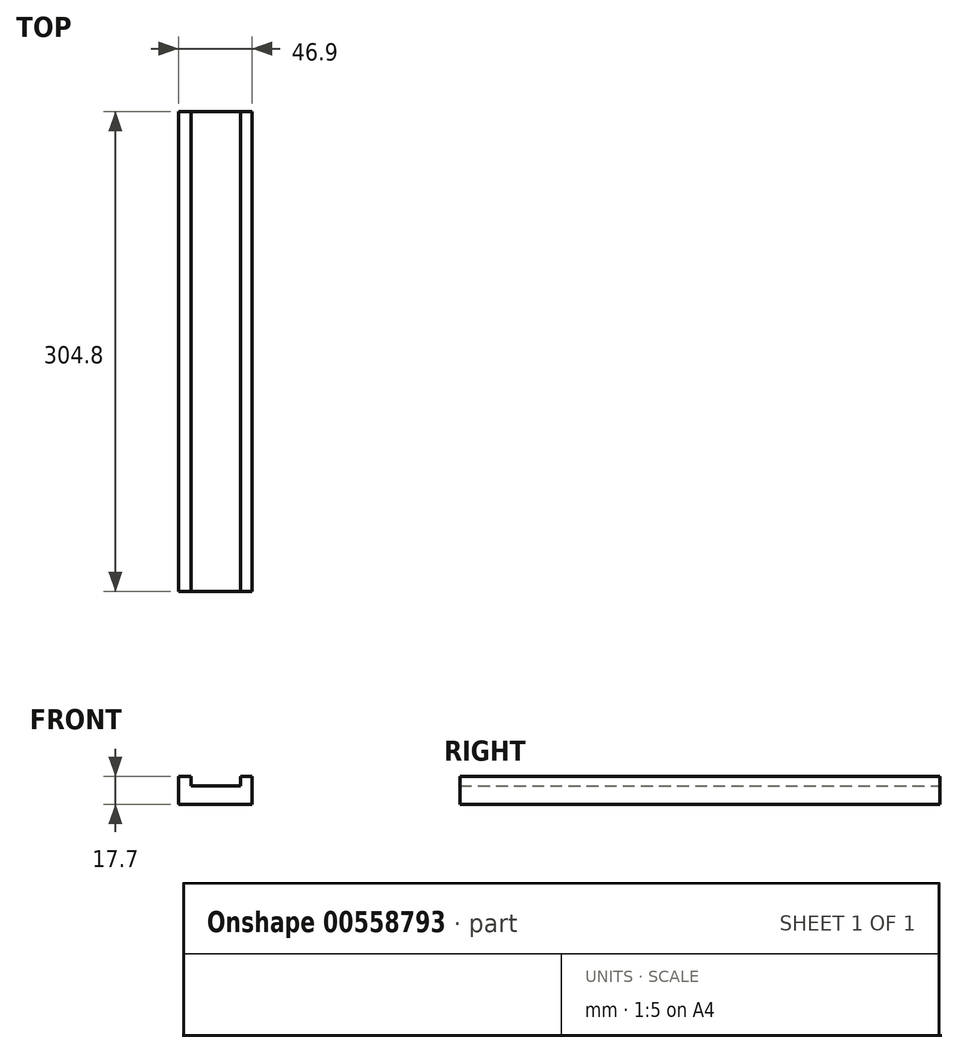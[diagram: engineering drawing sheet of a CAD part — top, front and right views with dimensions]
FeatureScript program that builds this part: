
annotation { "Feature Type Name" : "Feature", "Feature Type Description" : "" }
export const myFeature = defineFeature(function(context is Context, id is Id, definition is map)
    precondition{}
    {
        {
            var Q0;
            Q0=qCreatedBy(makeId("Front.planeOp"),FACE);
            var sketch = newSketch(context, id + "F0", { "sketchPlane" : qUnion([Q0])});
            skLineSegment(sketch, "E0", {"start": v(0, 0) * mm, "end": v(0, 74.52) * mm, "construction": true});
            skLineSegment(sketch, "E1", {"start": v(-15.26, 7.27) * mm, "end": v(15.98, 7.27) * mm});
            skLineSegment(sketch, "E2", {"start": v(15.98, 7.27) * mm, "end": v(15.98, 13.24) * mm});
            skLineSegment(sketch, "E3", {"start": v(15.98, 13.24) * mm, "end": v(23.45, 13.24) * mm});
            skLineSegment(sketch, "E4", {"start": v(-15.26, 7.27) * mm, "end": v(-15.26, 13.24) * mm});
            skLineSegment(sketch, "E5", {"start": v(-15.26, 13.24) * mm, "end": v(-23.45, 13.24) * mm});
            skLineSegment(sketch, "E6", {"start": v(23.45, 13.24) * mm, "end": v(23.45, -4.46) * mm});
            skLineSegment(sketch, "E7.MirrorCS", {"start": v(-23.45, 13.24) * mm, "end": v(-23.45, -4.46) * mm});
            skLineSegment(sketch, "E8", {"start": v(-23.45, -4.46) * mm, "end": v(23.45, -4.46) * mm});
            skLineSegment(sketch, "E9", {"start": v(0, 0) * mm, "end": v(56.54, 0) * mm, "construction": true});
            skSolve(sketch);
        }
        {
            var Q0;
            Q0 = qSketchRegion(id + "F0", true);
            extrude(context, id + "F1", {"entities" : qUnion([Q0]), "depth" : 304.8 * mm, "offsetDistance" : 25.4 * mm});
        }
    });
